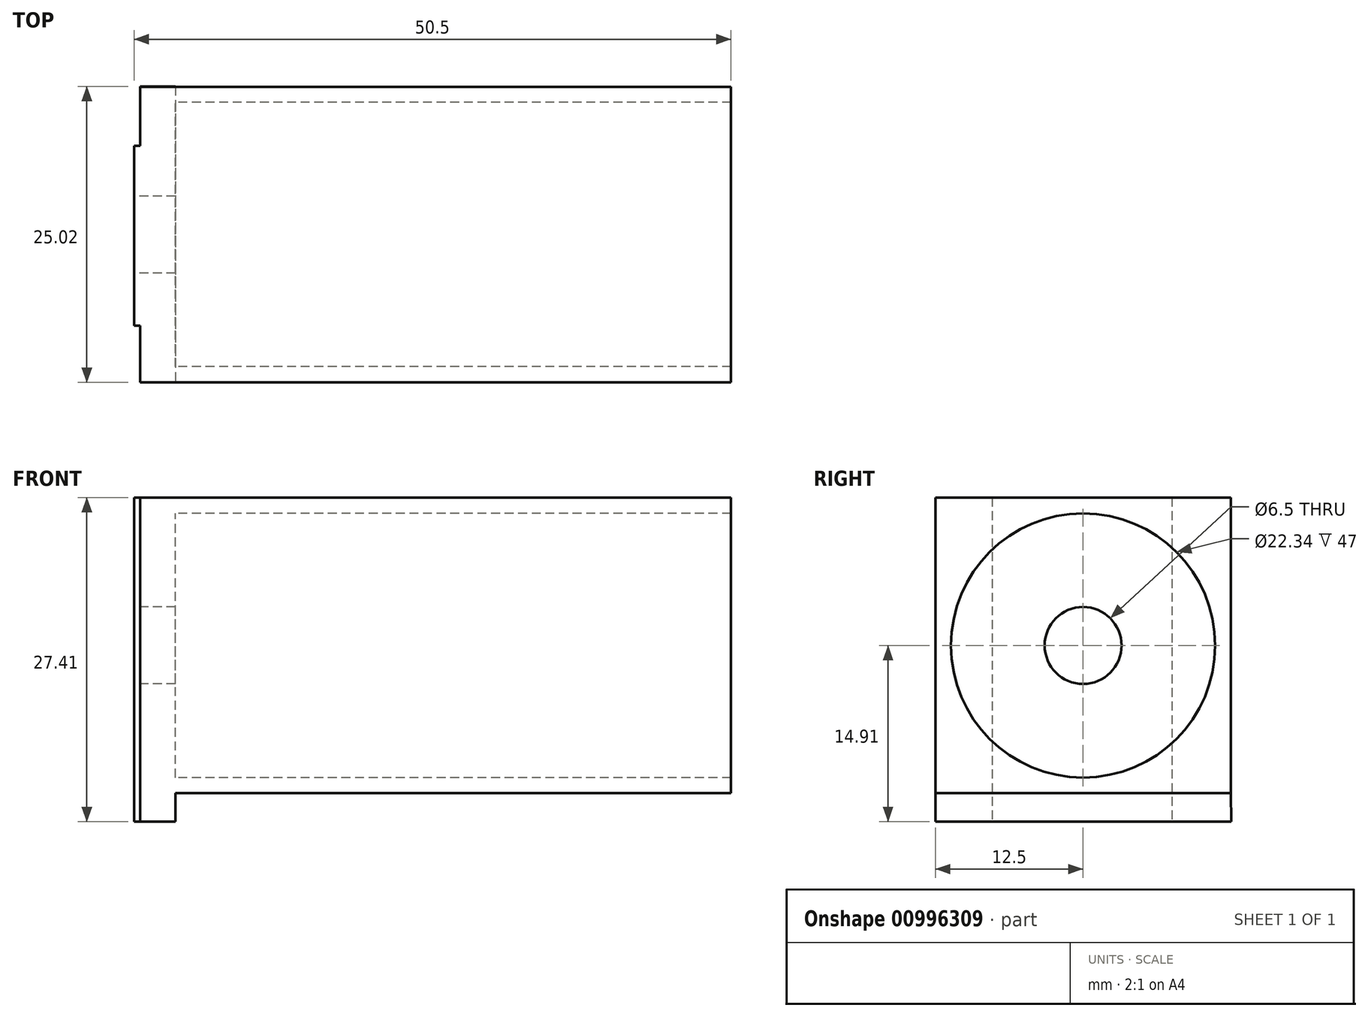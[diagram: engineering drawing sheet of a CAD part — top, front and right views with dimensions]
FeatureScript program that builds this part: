
annotation { "Feature Type Name" : "Feature", "Feature Type Description" : "" }
export const myFeature = defineFeature(function(context is Context, id is Id, definition is map)
    precondition{}
    {
        {
            var Q0;
            Q0=qCreatedBy(makeId("Right.planeOp"),FACE);
            var sketch = newSketch(context, id + "F0", { "sketchPlane" : qUnion([Q0])});
            skPoint(sketch, "E0.middle", {"position": v(0, 0) * mm});
            skCircle(sketch, "E1", {"center": v(0, 0) * mm, "radius": 3.25 * mm});
            skLineSegment(sketch, "E2.bottom", {"start": v(12.5, 12.5) * mm, "end": v(-12.5, 12.5) * mm});
            skLineSegment(sketch, "E2.top", {"start": v(12.5, -12.5) * mm, "end": v(-12.5, -12.5) * mm});
            skLineSegment(sketch, "E2.left", {"start": v(12.5, 12.5) * mm, "end": v(12.5, -12.5) * mm});
            skLineSegment(sketch, "E2.right", {"start": v(-12.5, 12.5) * mm, "end": v(-12.5, -12.5) * mm});
            skCircle(sketch, "E3", {"center": v(0, 0) * mm, "radius": 11.17 * mm});
            skLineSegment(sketch, "E4", {"start": v(12.52, -14.91) * mm, "end": v(-12.5, -14.91) * mm});
            skLineSegment(sketch, "E5", {"start": v(12.5, -12.5) * mm, "end": v(12.52, -14.91) * mm});
            skLineSegment(sketch, "E6", {"start": v(-12.5, -12.5) * mm, "end": v(-12.5, -14.91) * mm});
            skSolve(sketch);
        }
        {
            var Q0;
            Q0=makeQuery(id+"F0.imprint","IMPRINT",FACE,{"disambiguationData":[TD([[makeQuery(id+"F0.imprint","IMPRINT",EDGE,{"derivedFrom":sQuery(id+"F0.wireOp",EDGE,"E1")}),-1.0]])]});
            extrude(context, id + "F1", {"entities" : qUnion([Q0]), "depth" : 3 * mm, "offsetDistance" : 25 * mm});
        }
        {
            var Q0;
            Q0=makeQuery(id+"F0.imprint","IMPRINT",FACE,{"disambiguationData":[TD([[makeQuery(id+"F0.imprint","IMPRINT",EDGE,{"derivedFrom":sQuery(id+"F0.wireOp",EDGE,"E2.bottom")}),1.0]])]});
            extrude(context, id + "F2", {"entities" : qUnion([Q0]), "operationType" : NewBodyOperationType.ADD, "depth" : 50 * mm, "offsetDistance" : 25 * mm});
        }
        {
            var Q0;
            Q0=makeQuery(id+"F0.imprint","IMPRINT",FACE,{"disambiguationData":[TD([[makeQuery(id+"F0.imprint","IMPRINT",EDGE,{"derivedFrom":sQuery(id+"F0.wireOp",EDGE,"E2.top")}),1.0]])]});
            extrude(context, id + "F3", {"entities" : qUnion([Q0]), "operationType" : NewBodyOperationType.ADD, "depth" : 3 * mm, "offsetDistance" : 25 * mm});
        }
        {
            var Q0;
            {var subQ0=sQuery(id+"F0.wireOp",EDGE,"E2.top");var subQ1=sQuery(id+"F0.wireOp",EDGE,"E3");Q0=makeQuery(id+"F3.boolean.opBoolean","MERGE",FACE,{"derivedFrom":[makeQuery(id+"F2.boolean.opBoolean","MERGE",FACE,{"derivedFrom":[makeQuery(id+"F1.opExtrude","CAP_FACE",FACE,{"disambiguationData":[OSD([sQuery(id+"F0.wireOp",EDGE,"E1"),subQ1])],"isStart":true}),makeQuery(id+"F2.opExtrude","CAP_FACE",FACE,{"disambiguationData":[OSD([sQuery(id+"F0.wireOp",EDGE,"E2.bottom"),subQ0,sQuery(id+"F0.wireOp",EDGE,"E2.left"),sQuery(id+"F0.wireOp",EDGE,"E2.right"),subQ1])],"isStart":true})]}),makeQuery(id+"F3.opExtrude","CAP_FACE",FACE,{"disambiguationData":[OSD([subQ0,sQuery(id+"F0.wireOp",EDGE,"E4"),sQuery(id+"F0.wireOp",EDGE,"E5"),sQuery(id+"F0.wireOp",EDGE,"E6")])],"isStart":true})]});}
            var sketch = newSketch(context, id + "F4", { "sketchPlane" : qUnion([Q0])});
            skLineSegment(sketch, "E7", {"start": v(-7.5, 12.5) * mm, "end": v(-7.5, -14.91) * mm});
            skLineSegment(sketch, "E8", {"start": v(7.7, 12.5) * mm, "end": v(7.7, -14.91) * mm});
            skSolve(sketch);
        }
        {
            var Q0;
            {var subQ0=sQuery(id+"F4.wireOp",EDGE,"E7");Q0=makeQuery(id+"F4.imprint","IMPRINT",FACE,{"disambiguationData":[TD([[makeQuery(id+"F4.imprint","IMPRINT",EDGE,{"derivedFrom":subQ0}),1.0]])]});}
            extrude(context, id + "F5", {"entities" : qUnion([Q0]), "operationType" : NewBodyOperationType.ADD, "depth" : .5 * mm, "offsetDistance" : 25 * mm});
        }
    });
